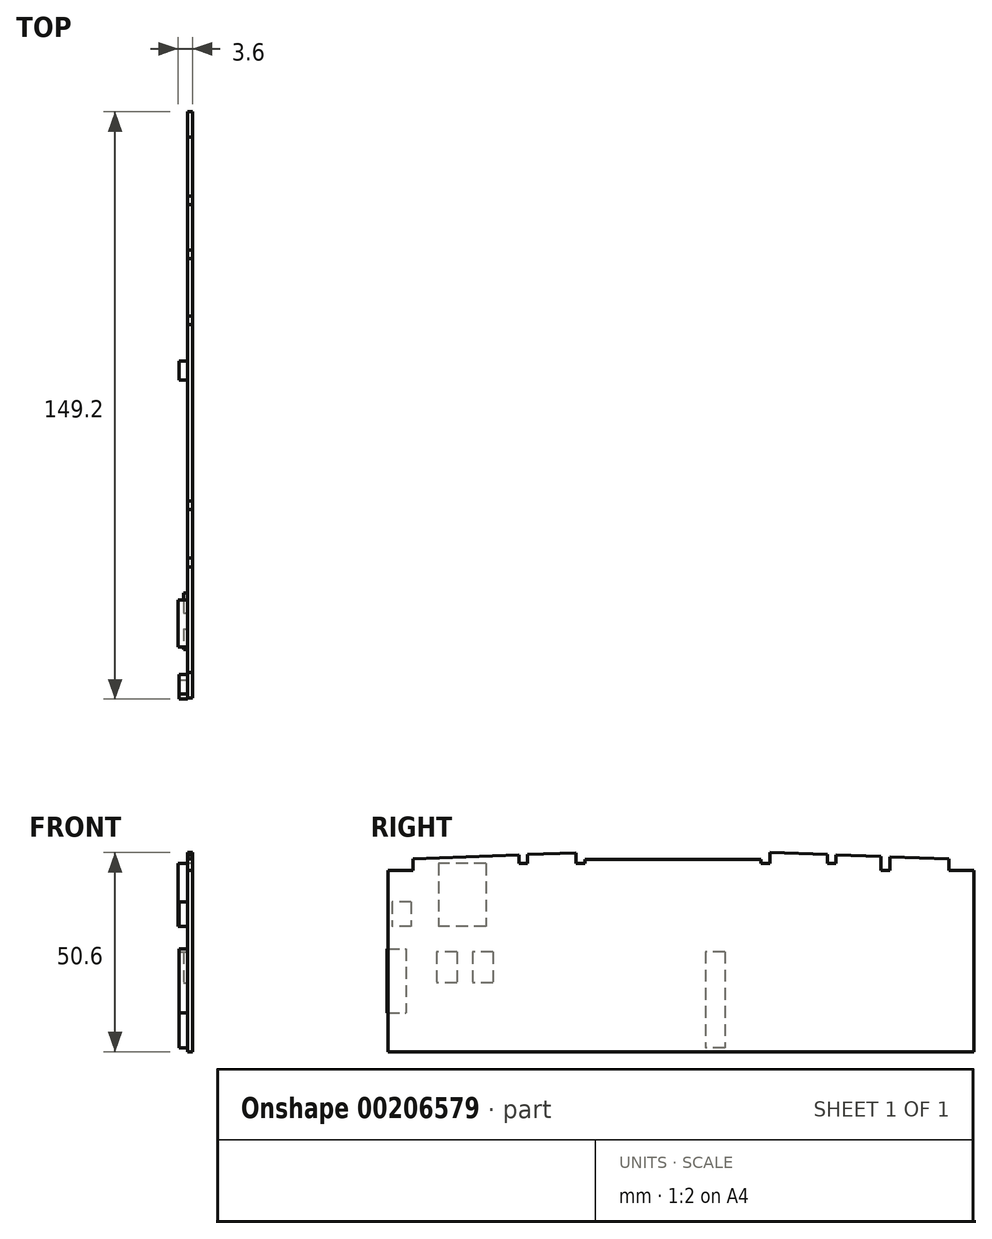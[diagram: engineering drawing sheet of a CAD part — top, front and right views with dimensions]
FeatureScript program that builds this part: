
annotation { "Feature Type Name" : "Feature", "Feature Type Description" : "" }
export const myFeature = defineFeature(function(context is Context, id is Id, definition is map)
    precondition{}
    {
        {
            var Q0;
            Q0=qCreatedBy(makeId("Right.planeOp"),FACE);
            var sketch = newSketch(context, id + "F0", { "sketchPlane" : qUnion([Q0])});
            skLineSegment(sketch, "E0", {"start": v(74.45, 46) * mm, "end": v(68.05, 46) * mm});
            skLineSegment(sketch, "E1", {"start": v(68.05, 46) * mm, "end": v(68.05, 49) * mm});
            skLineSegment(sketch, "E2", {"start": v(53.05, 46) * mm, "end": v(50.85, 46) * mm});
            skLineSegment(sketch, "E3", {"start": v(50.85, 46) * mm, "end": v(50.85, 49.6) * mm});
            skLineSegment(sketch, "E4", {"start": v(39.35, 50) * mm, "end": v(39.35, 47.8) * mm});
            skLineSegment(sketch, "E5", {"start": v(39.35, 47.8) * mm, "end": v(37.15, 47.8) * mm});
            skLineSegment(sketch, "E6", {"start": v(22.55, 50.6) * mm, "end": v(22.55, 47.8) * mm});
            skLineSegment(sketch, "E7", {"start": v(22.55, 47.8) * mm, "end": v(20.35, 47.8) * mm});
            skLineSegment(sketch, "E8", {"start": v(20.35, 47.8) * mm, "end": v(20.35, 48.9) * mm});
            skLineSegment(sketch, "E9", {"start": v(-64.2, 43) * mm, "end": v(-64.2, 43) * mm});
            skLineSegment(sketch, "E10", {"start": v(-68.05, 49) * mm, "end": v(-68.05, 46) * mm});
            skLineSegment(sketch, "E11", {"start": v(-68.05, 46) * mm, "end": v(-74.45, 46) * mm});
            skLineSegment(sketch, "E12", {"start": v(74.45, 46) * mm, "end": v(74.45, 0) * mm});
            skLineSegment(sketch, "E13", {"start": v(74.45, 0) * mm, "end": v(-74.45, 0) * mm});
            skLineSegment(sketch, "E14", {"start": v(-74.45, 0) * mm, "end": v(-74.45, 46) * mm});
            skLineSegment(sketch, "E15", {"start": v(22.55, 50.6) * mm, "end": v(37.15, 50.09) * mm});
            skLineSegment(sketch, "E16", {"start": v(39.35, 50) * mm, "end": v(50.85, 49.6) * mm});
            skLineSegment(sketch, "E17", {"start": v(53.05, 49.53) * mm, "end": v(68.05, 49) * mm});
            skLineSegment(sketch, "E18", {"start": v(-41.15, 47.8) * mm, "end": v(-41.15, 49.97) * mm});
            skLineSegment(sketch, "E19", {"start": v(-41.15, 49.97) * mm, "end": v(-68.05, 49) * mm});
            skPoint(sketch, "E20", {"position": v(0, 0) * mm});
            skLineSegment(sketch, "E21", {"start": v(53.05, 49.53) * mm, "end": v(53.05, 46) * mm});
            skLineSegment(sketch, "E22", {"start": v(53.05, 49.53) * mm, "end": v(50.85, 49.6) * mm, "construction": true});
            skLineSegment(sketch, "E23", {"start": v(39.35, 50) * mm, "end": v(37.15, 50.09) * mm, "construction": true});
            skLineSegment(sketch, "E24", {"start": v(37.15, 50.09) * mm, "end": v(37.15, 47.8) * mm});
            skLineSegment(sketch, "E25", {"start": v(-68.05, 49) * mm, "end": v(-26.65, 49) * mm, "construction": true});
            skLineSegment(sketch, "E26", {"start": v(-26.65, 49) * mm, "end": v(-26.65, 50.5) * mm, "construction": true});
            skLineSegment(sketch, "E27", {"start": v(-26.65, 50.5) * mm, "end": v(-41.15, 49.97) * mm, "construction": true});
            skLineSegment(sketch, "E28", {"start": v(-41.15, 47.8) * mm, "end": v(-38.95, 47.8) * mm});
            skLineSegment(sketch, "E29", {"start": v(-38.95, 47.8) * mm, "end": v(-38.95, 50.05) * mm});
            skLineSegment(sketch, "E30", {"start": v(-38.95, 50.05) * mm, "end": v(-26.65, 50.5) * mm});
            skLineSegment(sketch, "E31", {"start": v(-26.65, 50.5) * mm, "end": v(-26.65, 47.8) * mm});
            skLineSegment(sketch, "E32", {"start": v(-26.65, 47.8) * mm, "end": v(-24.45, 47.8) * mm});
            skLineSegment(sketch, "E33", {"start": v(-24.45, 47.8) * mm, "end": v(-24.45, 48.9) * mm});
            skLineSegment(sketch, "E34", {"start": v(-24.45, 48.9) * mm, "end": v(20.35, 48.9) * mm});
            skLineSegment(sketch, "E35", {"start": v(37.15, 47.8) * mm, "end": v(22.55, 47.8) * mm, "construction": true});
            skLineSegment(sketch, "E36", {"start": v(20.35, 47.8) * mm, "end": v(-24.45, 47.8) * mm, "construction": true});
            skLineSegment(sketch, "E37", {"start": v(-26.65, 47.8) * mm, "end": v(-38.95, 47.8) * mm, "construction": true});
            skSolve(sketch);
        }
        {
            var Q0;
            Q0=makeQuery(id+"F0.imprint","IMPRINT",FACE,{"disambiguationData":[TD([[makeQuery(id+"F0.imprint","IMPRINT",EDGE,{"derivedFrom":sQuery(id+"F0.wireOp",EDGE,"E0")}),1.0]])]});
            extrude(context, id + "F1", {"entities" : qUnion([Q0]), "depth" : 1.2 * mm});
        }
        {
            var Q0;
            Q0=makeQuery(id+"F1.opExtrude","CAP_FACE",FACE,{"disambiguationData":[OSD([sQuery(id+"F0.wireOp",EDGE,"E0"),sQuery(id+"F0.wireOp",EDGE,"E1"),sQuery(id+"F0.wireOp",EDGE,"E2"),sQuery(id+"F0.wireOp",EDGE,"E3"),sQuery(id+"F0.wireOp",EDGE,"E4"),sQuery(id+"F0.wireOp",EDGE,"E5"),sQuery(id+"F0.wireOp",EDGE,"E6"),sQuery(id+"F0.wireOp",EDGE,"E7"),sQuery(id+"F0.wireOp",EDGE,"E8"),sQuery(id+"F0.wireOp",EDGE,"E10"),sQuery(id+"F0.wireOp",EDGE,"E11"),sQuery(id+"F0.wireOp",EDGE,"E12"),sQuery(id+"F0.wireOp",EDGE,"E13"),sQuery(id+"F0.wireOp",EDGE,"E14"),sQuery(id+"F0.wireOp",EDGE,"E15"),sQuery(id+"F0.wireOp",EDGE,"E16"),sQuery(id+"F0.wireOp",EDGE,"E17"),sQuery(id+"F0.wireOp",EDGE,"E18"),sQuery(id+"F0.wireOp",EDGE,"E19"),sQuery(id+"F0.wireOp",EDGE,"E21"),sQuery(id+"F0.wireOp",EDGE,"E24"),sQuery(id+"F0.wireOp",EDGE,"E28"),sQuery(id+"F0.wireOp",EDGE,"E29"),sQuery(id+"F0.wireOp",EDGE,"E30"),sQuery(id+"F0.wireOp",EDGE,"E31"),sQuery(id+"F0.wireOp",EDGE,"E32"),sQuery(id+"F0.wireOp",EDGE,"E33"),sQuery(id+"F0.wireOp",EDGE,"E34")])],"isStart":true});
            var sketch = newSketch(context, id + "F2", { "sketchPlane" : qUnion([Q0])});
            skLineSegment(sketch, "E38.bottom", {"start": v(49.55, 47.8) * mm, "end": v(61.55, 47.8) * mm});
            skLineSegment(sketch, "E38.top", {"start": v(49.55, 31.8) * mm, "end": v(61.55, 31.8) * mm});
            skLineSegment(sketch, "E38.left", {"start": v(49.55, 47.8) * mm, "end": v(49.55, 31.8) * mm});
            skLineSegment(sketch, "E38.right", {"start": v(61.55, 47.8) * mm, "end": v(61.55, 31.8) * mm});
            skLineSegment(sketch, "E39.bottom", {"start": v(68.55, 38) * mm, "end": v(73.45, 38) * mm});
            skLineSegment(sketch, "E39.top", {"start": v(68.55, 31.8) * mm, "end": v(73.45, 31.8) * mm});
            skLineSegment(sketch, "E39.left", {"start": v(68.55, 38) * mm, "end": v(68.55, 31.8) * mm});
            skLineSegment(sketch, "E39.right", {"start": v(73.45, 38) * mm, "end": v(73.45, 31.8) * mm});
            skLineSegment(sketch, "E40", {"start": v(61.55, 31.8) * mm, "end": v(68.55, 31.8) * mm, "construction": true});
            skLineSegment(sketch, "E41.bottom", {"start": v(74.75, 26.1) * mm, "end": v(69.85, 26.1) * mm});
            skLineSegment(sketch, "E41.top", {"start": v(74.75, 9.9) * mm, "end": v(69.85, 9.9) * mm});
            skLineSegment(sketch, "E41.left", {"start": v(74.75, 26.1) * mm, "end": v(74.75, 9.9) * mm});
            skLineSegment(sketch, "E41.right", {"start": v(69.85, 26.1) * mm, "end": v(69.85, 9.9) * mm});
            skLineSegment(sketch, "E42.bottom", {"start": v(-11.15, 25.4) * mm, "end": v(-6.25, 25.4) * mm});
            skLineSegment(sketch, "E42.top", {"start": v(-11.15, 1) * mm, "end": v(-6.25, 1) * mm});
            skLineSegment(sketch, "E42.left", {"start": v(-11.15, 25.4) * mm, "end": v(-11.15, 1) * mm});
            skLineSegment(sketch, "E42.right", {"start": v(-6.25, 25.4) * mm, "end": v(-6.25, 1) * mm});
            skLineSegment(sketch, "E43.bottom", {"start": v(56.95, 25.3) * mm, "end": v(62.15, 25.3) * mm});
            skLineSegment(sketch, "E43.top", {"start": v(56.95, 17.5) * mm, "end": v(62.15, 17.5) * mm});
            skLineSegment(sketch, "E43.left", {"start": v(56.95, 25.3) * mm, "end": v(56.95, 17.5) * mm});
            skLineSegment(sketch, "E43.right", {"start": v(62.15, 25.3) * mm, "end": v(62.15, 17.5) * mm});
            skLineSegment(sketch, "E44.bottom", {"start": v(47.75, 25.3) * mm, "end": v(52.95, 25.3) * mm});
            skLineSegment(sketch, "E44.top", {"start": v(47.75, 17.5) * mm, "end": v(52.95, 17.5) * mm});
            skLineSegment(sketch, "E44.left", {"start": v(47.75, 25.3) * mm, "end": v(47.75, 17.5) * mm});
            skLineSegment(sketch, "E44.right", {"start": v(52.95, 25.3) * mm, "end": v(52.95, 17.5) * mm});
            skLineSegment(sketch, "E45", {"start": v(52.95, 25.3) * mm, "end": v(56.95, 25.3) * mm, "construction": true});
            skSolve(sketch);
        }
        {
            var Q0;
            Q0=makeQuery(id+"F2.imprint","IMPRINT",FACE,{"disambiguationData":[TD([[makeQuery(id+"F2.imprint","IMPRINT",EDGE,{"derivedFrom":sQuery(id+"F2.wireOp",EDGE,"E39.bottom")}),-1.0]])]});
            var Q1;
            {var subQ0=sQuery(id+"F2.wireOp",EDGE,"E41.right");Q1=makeQuery(id+"F2.imprint","IMPRINT",FACE,{"disambiguationData":[TD([[makeQuery(id+"F2.imprint","IMPRINT",EDGE,{"derivedFrom":subQ0}),1.0]])]});}
            var Q2;
            {var subQ0=sQuery(id+"F2.wireOp",EDGE,"E41.left");Q2=makeQuery(id+"F2.imprint","IMPRINT",FACE,{"disambiguationData":[TD([[makeQuery(id+"F2.imprint","IMPRINT",EDGE,{"derivedFrom":subQ0}),-1.0]])]});}
            var Q3;
            Q3=makeQuery(id+"F2.imprint","IMPRINT",FACE,{"disambiguationData":[TD([[makeQuery(id+"F2.imprint","IMPRINT",EDGE,{"derivedFrom":sQuery(id+"F2.wireOp",EDGE,"E42.bottom")}),-1.0]])]});
            extrude(context, id + "F4", {"entities" : qUnion([Q0, Q1, Q2, Q3]), "operationType" : NewBodyOperationType.ADD, "depth" : 2.2 * mm});
        }
        {
            var Q0;
            Q0=makeQuery(id+"F2.imprint","IMPRINT",FACE,{"disambiguationData":[TD([[makeQuery(id+"F2.imprint","IMPRINT",EDGE,{"derivedFrom":sQuery(id+"F2.wireOp",EDGE,"E38.bottom")}),-1.0]])]});
            extrude(context, id + "F5", {"entities" : qUnion([Q0]), "operationType" : NewBodyOperationType.ADD, "depth" : 2.4 * mm});
        }
        {
            var Q0;
            Q0=makeQuery(id+"F2.imprint","IMPRINT",FACE,{"disambiguationData":[TD([[makeQuery(id+"F2.imprint","IMPRINT",EDGE,{"derivedFrom":sQuery(id+"F2.wireOp",EDGE,"E44.bottom")}),-1.0]])]});
            var Q1;
            Q1=makeQuery(id+"F2.imprint","IMPRINT",FACE,{"disambiguationData":[TD([[makeQuery(id+"F2.imprint","IMPRINT",EDGE,{"derivedFrom":sQuery(id+"F2.wireOp",EDGE,"E43.bottom")}),-1.0]])]});
            extrude(context, id + "F6", {"entities" : qUnion([Q0, Q1]), "operationType" : NewBodyOperationType.ADD, "depth" : 1 * mm});
        }
    });
